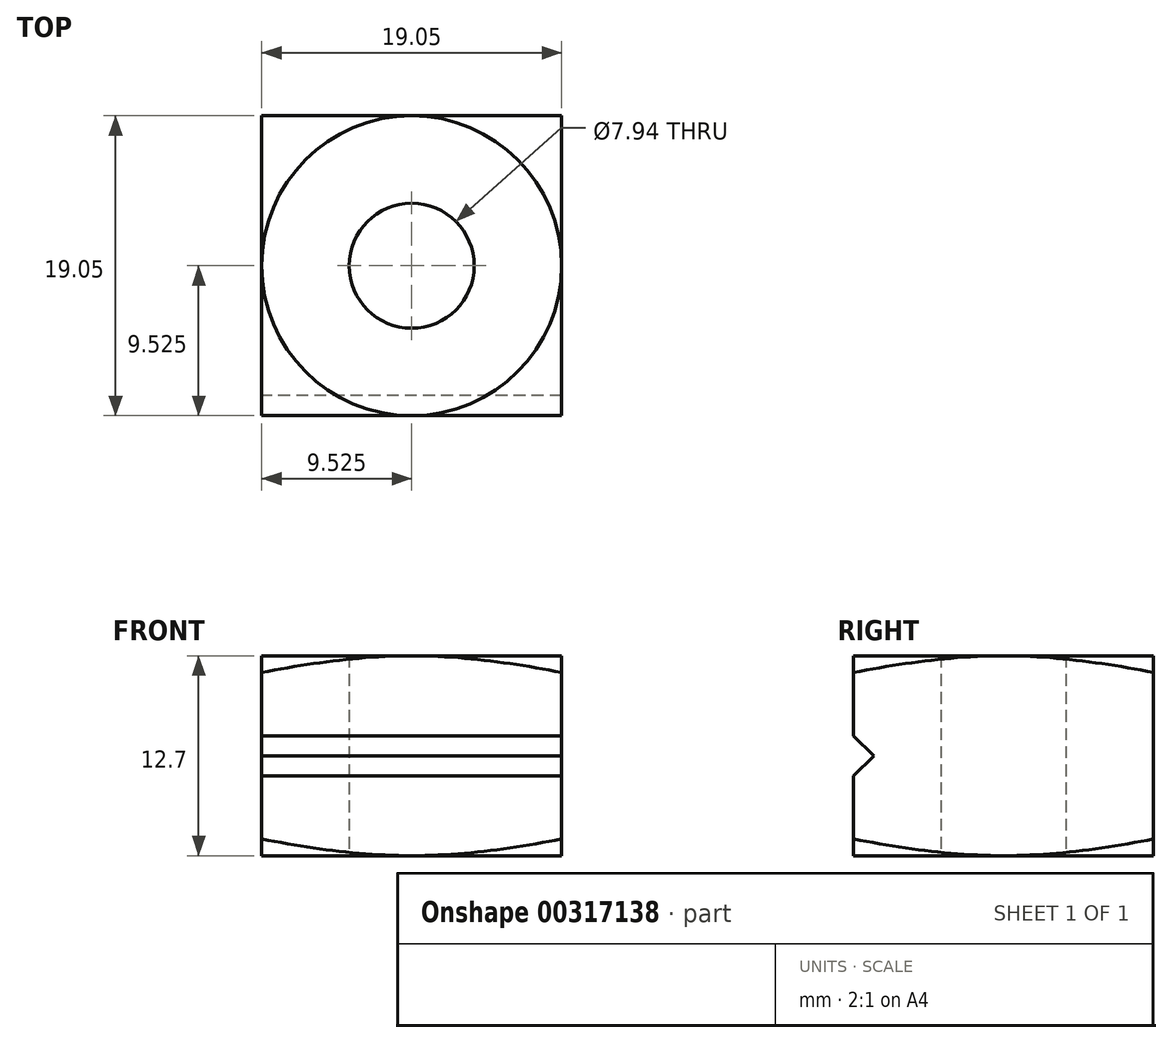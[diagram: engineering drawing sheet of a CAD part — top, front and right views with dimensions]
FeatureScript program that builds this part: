
annotation { "Feature Type Name" : "Feature", "Feature Type Description" : "" }
export const myFeature = defineFeature(function(context is Context, id is Id, definition is map)
    precondition{}
    {
        {
            var Q0;
            Q0=qCreatedBy(makeId("Top.planeOp"),FACE);
            var sketch = newSketch(context, id + "F0", { "sketchPlane" : qUnion([Q0])});
            skLineSegment(sketch, "E0.bottom", {"start": v(0, 0) * mm, "end": v(19.05, 0) * mm});
            skLineSegment(sketch, "E0.top", {"start": v(0, 19.05) * mm, "end": v(19.05, 19.05) * mm});
            skLineSegment(sketch, "E0.left", {"start": v(0, 0) * mm, "end": v(0, 19.05) * mm});
            skLineSegment(sketch, "E0.right", {"start": v(19.05, 0) * mm, "end": v(19.05, 19.05) * mm});
            skSolve(sketch);
        }
        {
            var Q0;
            Q0=qSketchRegion(id+"F0",true);
            extrude(context, id + "F1", {"entities" : qUnion([Q0]), "depth" : 12.7 * mm});
        }
        {
            var Q0;
            Q0=makeQuery(id+"F1.opExtrude","SWEPT_FACE",FACE,{"disambiguationData":[OSD([sQuery(id+"F0.wireOp",EDGE,"E0.left")])]});
            var sketch = newSketch(context, id + "F2", { "sketchPlane" : qUnion([Q0])});
            skLineSegment(sketch, "E1", {"start": v(-1.27, 6.35) * mm, "end": v(0, 5.08) * mm});
            skPoint(sketch, "E1.startSnap0", {"position": v(0, 6.35) * mm});
            skLineSegment(sketch, "E2", {"start": v(-1.27, 6.35) * mm, "end": v(0, 7.62) * mm});
            skLineSegment(sketch, "E3", {"start": v(0, 7.62) * mm, "end": v(0, 5.08) * mm});
            skLineSegment(sketch, "E4", {"start": v(0, 6.35) * mm, "end": v(-1.27, 6.35) * mm, "construction": true});
            skSolve(sketch);
        }
        {
            var Q0;
            Q0=qSketchRegion(id+"F2",true);
            extrude(context, id + "F3", {"entities" : qUnion([Q0]), "operationType" : NewBodyOperationType.REMOVE, "oppositeDirection" : true, "depth" : 19.05 * mm});
        }
        {
            var Q0;
            Q0=makeQuery(id+"F1.opExtrude","SWEPT_FACE",FACE,{"disambiguationData":[OSD([sQuery(id+"F0.wireOp",EDGE,"E0.left")])]});
            var Q1;
            Q1=makeQuery(id+"F1.opExtrude","SWEPT_FACE",FACE,{"disambiguationData":[OSD([sQuery(id+"F0.wireOp",EDGE,"E0.right")])]});
            cPlane(context, id + "F4", {"entities" : qUnion([Q0, Q1]), "cplaneType" : CPlaneType.MID_PLANE, "offset" : 25.4 * mm, "width" : 152.4 * mm, "height" : 152.4 * mm});
        }
        {
            var Q0;
            Q0=qCreatedBy(id+"F4.planeOp",FACE);
            var sketch = newSketch(context, id + "F5", { "sketchPlane" : qUnion([Q0])});
            skLineSegment(sketch, "E5", {"start": v(0, 0) * mm, "end": v(8.48, 2.27) * mm});
            skLineSegment(sketch, "E6", {"start": v(8.48, 2.27) * mm, "end": v(8.48, 0) * mm});
            skLineSegment(sketch, "E7", {"start": v(8.48, 0) * mm, "end": v(0, 0) * mm});
            skSolve(sketch);
        }
        {
            var Q0;
            Q0=makeQuery(id+"F1.opExtrude","CAP_FACE",FACE,{"disambiguationData":[OSD([sQuery(id+"F0.wireOp",EDGE,"E0.bottom"),sQuery(id+"F0.wireOp",EDGE,"E0.top"),sQuery(id+"F0.wireOp",EDGE,"E0.left"),sQuery(id+"F0.wireOp",EDGE,"E0.right")])],"isStart":true});
            var sketch = newSketch(context, id + "F6", { "sketchPlane" : qUnion([Q0])});
            skCircle(sketch, "E8", {"center": v(9.52, -9.53) * mm, "radius": 3.97 * mm});
            skPoint(sketch, "E8.centerSnap0", {"position": v(19.05, -9.53) * mm});
            skPoint(sketch, "E8.centerSnap1", {"position": v(9.52, -19.05) * mm});
            skSolve(sketch);
        }
        {
            var Q0;
            Q0=qSketchRegion(id+"F6",true);
            extrude(context, id + "F7", {"entities" : qUnion([Q0]), "operationType" : NewBodyOperationType.REMOVE, "oppositeDirection" : true, "depth" : 19.05 * mm});
        }
        {
            var Q0;
            Q0=qCreatedBy(id+"F4.planeOp",FACE);
            var sketch = newSketch(context, id + "F8", { "sketchPlane" : qUnion([Q0])});
            skPoint(sketch, "E9.0", {"position": v(0, 12.7) * mm});
            skLineSegment(sketch, "E10", {"start": v(-19.05, 12.7) * mm, "end": v(0, 12.7) * mm, "construction": true});
            skLineSegment(sketch, "E11", {"start": v(-19.05, 12.7) * mm, "end": v(-32.24, 16.24) * mm});
            skLineSegment(sketch, "E12", {"start": v(-32.24, 16.24) * mm, "end": v(-32.24, 9.16) * mm});
            skLineSegment(sketch, "E13", {"start": v(-32.24, 9.16) * mm, "end": v(-19.05, 12.7) * mm});
            skLineSegment(sketch, "E14", {"start": v(-19.05, 12.7) * mm, "end": v(-32.24, 12.7) * mm, "construction": true});
            skSolve(sketch);
        }
        {
            var Q0;
            Q0=makeQuery(id+"F8.imprint","IMPRINT",FACE,{"disambiguationData":[TD([[makeQuery(id+"F8.imprint","IMPRINT",EDGE,{"derivedFrom":sQuery(id+"F8.wireOp",EDGE,"E11")}),1.0]])]});
            var Q1;
            Q1=makeQuery(id+"F5.imprint","IMPRINT",FACE,{"disambiguationData":[TD([[makeQuery(id+"F5.imprint","IMPRINT",EDGE,{"derivedFrom":sQuery(id+"F5.wireOp",EDGE,"E5")}),-1.0]])]});
            var Q2;
            Q2=makeQuery(id+"F7.boolean.opBoolean","INTERSECT",EDGE,{"derivedFrom":[makeQuery(id+"F1.opExtrude","CAP_FACE",FACE,{"disambiguationData":[OSD([sQuery(id+"F0.wireOp",EDGE,"E0.bottom"),sQuery(id+"F0.wireOp",EDGE,"E0.top"),sQuery(id+"F0.wireOp",EDGE,"E0.left"),sQuery(id+"F0.wireOp",EDGE,"E0.right")])],"isStart":false}),makeQuery(id+"F7.opExtrude","SWEPT_FACE",FACE,{"disambiguationData":[OSD([sQuery(id+"F6.wireOp",EDGE,"E8")])]})]});
            revolve(context, id + "F9", {"operationType" : NewBodyOperationType.REMOVE, "entities" : qUnion([Q0, Q1]), "axis" : qUnion([Q2]), "revolveType" : RevolveType.FULL, "oppositeDirection" : true});
        }
    });
